# Revit family: LC4
name_source: partatom
category: Lighting Fixtures
revit_build: Autodesk Revit 2014 (Build: 20130308_1515(x64)
units: mm (PartAtom-declared; Revit-internal decimal feet)

## types (6) — shared parameters
Apparent Load = 0 VA
Assembly Code = D5020200
Color Filter = 16777215
Default Elevation = 48"
Description = 4in LED Downlight
Dimming Lamp Color Temperature Shift = <None>
Emit Shape Visible in Rendering = No
Emit from Circle Diameter = 4"
Glass = Hubbell - White Glass
Hardware Finish = Steel - Hubbell
Lamp = LED
Load Classification = Lighting
Manufacturer = Prescolite
Model = LC4SL
Photometric Notes = More IES files download on Photometric Web Link
Photometric Web Link = https://www.hubbell.com
Power Factor = 1
Product Documentation Link = https://hubbellcdn.com
Product Page URL = https://www.hubbell.com
Tilt Angle = -90.00°
URL = https://www.hubbell.com
Voltage = 120 V
Wattage Comments = 13.4, 17.8 & 22.2

## per-type parameters (varying)
| type | Photometric Web File |
| LC4SL-4LCSL10L27K8 | LC4SL-4LCSL10L27K8.ies |
| LC4SL-4LCSL14L27K8 | LC4SL-4LCSL14L27K8.ies |
| LC4SL-4LCSL18L35K8 | LC4SL-4LCSL18L35K8.ies |
| LC4SL-4LCSL10L50K8 | LC4SL-4LCSL10L50K8.ies |
| LC4SL-4LCSL14L40K8 | LC4SL-4LCSL14L40K8.ies |
| LC4SL-4LCSL18L40K8WW | LC4SL-4LCSL18L40K8WW.IES |

## geometry (parser evidence)
native form markers: Blend x4, Sweep x1
no freeform markers — native parametric forms only
